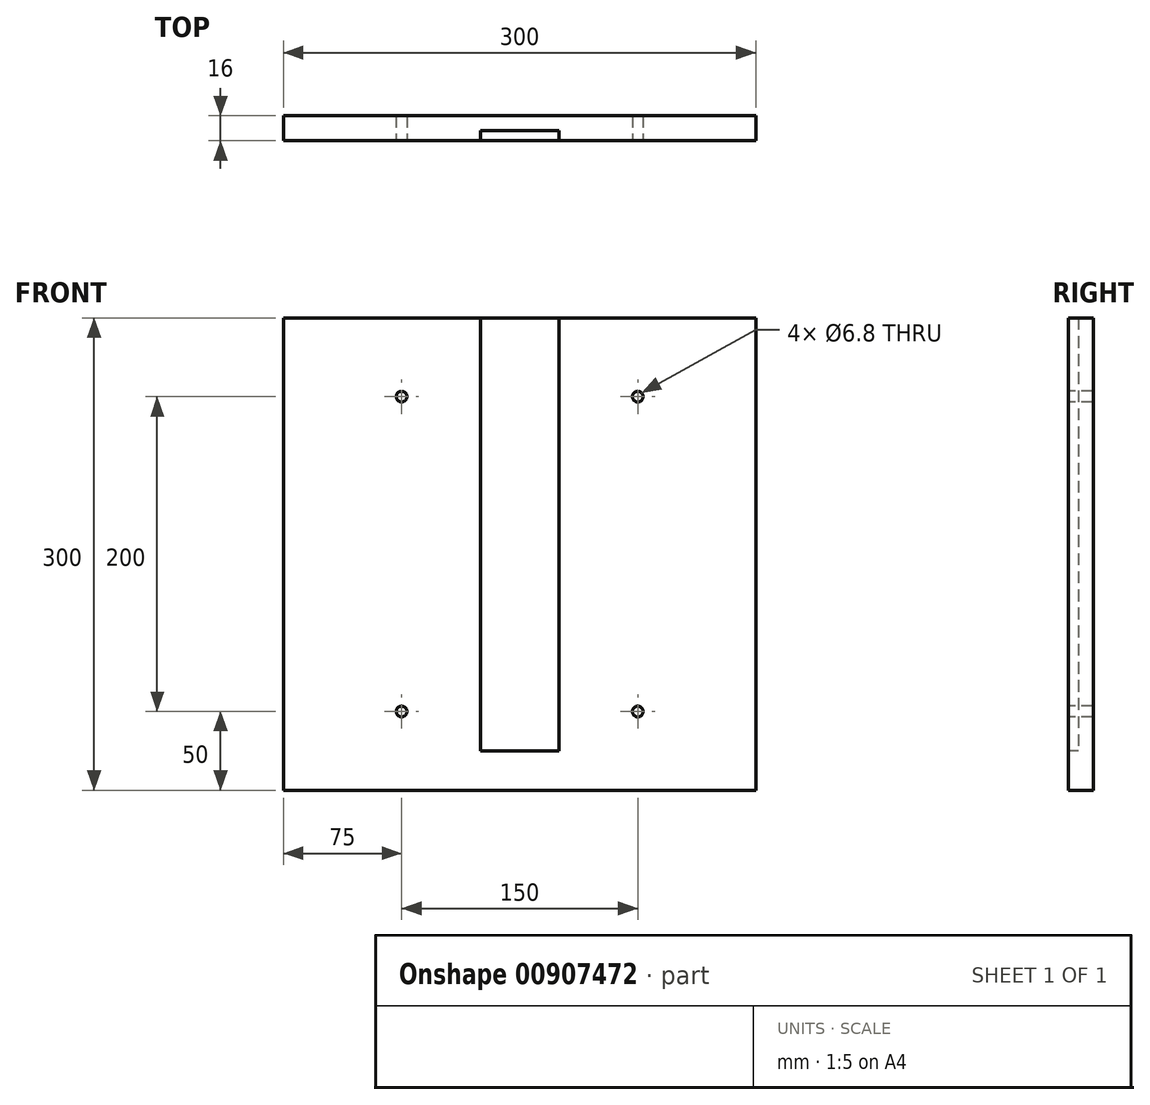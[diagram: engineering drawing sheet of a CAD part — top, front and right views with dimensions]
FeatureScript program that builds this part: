
annotation { "Feature Type Name" : "Feature", "Feature Type Description" : "" }
export const myFeature = defineFeature(function(context is Context, id is Id, definition is map)
    precondition{}
    {
        {
            var Q0;
            Q0=qCreatedBy(makeId("Front.planeOp"),FACE);
            var sketch = newSketch(context, id + "F0", { "sketchPlane" : qUnion([Q0])});
            skLineSegment(sketch, "E0.bottom", {"start": v(-155, 150) * mm, "end": v(155, 150) * mm});
            skLineSegment(sketch, "E0.top", {"start": v(-155, -150) * mm, "end": v(155, -150) * mm});
            skLineSegment(sketch, "E0.left", {"start": v(-155, 150) * mm, "end": v(-155, -150) * mm});
            skLineSegment(sketch, "E0.right", {"start": v(155, 150) * mm, "end": v(155, -150) * mm});
            skLineSegment(sketch, "E1", {"start": v(-155, 150) * mm, "end": v(155, -150) * mm, "construction": true});
            skSolve(sketch);
        }
        {
            var Q0;
            Q0=makeQuery(id+"F0.imprint","IMPRINT",FACE,{"disambiguationData":[TD([[makeQuery(id+"F0.imprint","IMPRINT",EDGE,{"derivedFrom":sQuery(id+"F0.wireOp",EDGE,"E0.bottom")}),-1.0]])]});
            extrude(context, id + "F1", {"entities" : qUnion([Q0]), "depth" : 16 * mm, "offsetDistance" : 25 * mm});
        }
        {
            var Q0;
            Q0=makeQuery(id+"F1.opExtrude","CAP_FACE",FACE,{"disambiguationData":[OSD([sQuery(id+"F0.wireOp",EDGE,"E0.bottom"),sQuery(id+"F0.wireOp",EDGE,"E0.top"),sQuery(id+"F0.wireOp",EDGE,"E0.left"),sQuery(id+"F0.wireOp",EDGE,"E0.right")])],"isStart":false});
            var sketch = newSketch(context, id + "F2", { "sketchPlane" : qUnion([Q0])});
            skLineSegment(sketch, "E2.bottom", {"start": v(155, 150) * mm, "end": v(150, 150) * mm});
            skLineSegment(sketch, "E2.top", {"start": v(155, -150) * mm, "end": v(150, -150) * mm});
            skLineSegment(sketch, "E2.left", {"start": v(155, 150) * mm, "end": v(155, -150) * mm});
            skLineSegment(sketch, "E2.right", {"start": v(150, 150) * mm, "end": v(150, -150) * mm});
            skLineSegment(sketch, "E3.bottom", {"start": v(-155, -150) * mm, "end": v(-150, -150) * mm});
            skLineSegment(sketch, "E3.top", {"start": v(-155, 150) * mm, "end": v(-150, 150) * mm});
            skLineSegment(sketch, "E3.left", {"start": v(-155, -150) * mm, "end": v(-155, 150) * mm});
            skLineSegment(sketch, "E3.right", {"start": v(-150, -150) * mm, "end": v(-150, 150) * mm});
            skSolve(sketch);
        }
        {
            var Q0;
            Q0 = qSketchRegion(id + "F2", true);
            extrude(context, id + "F3", {"entities" : qUnion([Q0]), "operationType" : NewBodyOperationType.REMOVE, "endBound" : BoundingType.THROUGH_ALL, "oppositeDirection" : true, "depth" : 25 * mm, "offsetDistance" : 25 * mm});
        }
        {
            var Q0;
            Q0=makeQuery(id+"F1.opExtrude","CAP_FACE",FACE,{"disambiguationData":[OSD([sQuery(id+"F0.wireOp",EDGE,"E0.bottom"),sQuery(id+"F0.wireOp",EDGE,"E0.top"),sQuery(id+"F0.wireOp",EDGE,"E0.left"),sQuery(id+"F0.wireOp",EDGE,"E0.right")])],"isStart":false});
            var sketch = newSketch(context, id + "F4", { "sketchPlane" : qUnion([Q0])});
            skLineSegment(sketch, "E4.bottom", {"start": v(-25, 150) * mm, "end": v(25, 150) * mm});
            skLineSegment(sketch, "E4.top", {"start": v(-25, -125) * mm, "end": v(25, -125) * mm});
            skLineSegment(sketch, "E4.left", {"start": v(-25, 150) * mm, "end": v(-25, -125) * mm});
            skLineSegment(sketch, "E4.right", {"start": v(25, 150) * mm, "end": v(25, -125) * mm});
            skSolve(sketch);
        }
        {
            var Q0;
            Q0 = qSketchRegion(id + "F4", true);
            extrude(context, id + "F5", {"entities" : qUnion([Q0]), "operationType" : NewBodyOperationType.REMOVE, "oppositeDirection" : true, "depth" : 6.5 * mm, "offsetDistance" : 25 * mm});
        }
        {
            var Q0;
            Q0=makeQuery(id+"F1.opExtrude","CAP_FACE",FACE,{"disambiguationData":[OSD([sQuery(id+"F0.wireOp",EDGE,"E0.bottom"),sQuery(id+"F0.wireOp",EDGE,"E0.top"),sQuery(id+"F0.wireOp",EDGE,"E0.left"),sQuery(id+"F0.wireOp",EDGE,"E0.right")])],"isStart":false});
            var sketch = newSketch(context, id + "F6", { "sketchPlane" : qUnion([Q0])});
            skPoint(sketch, "E5", {"position": v(-75, 100) * mm});
            skPoint(sketch, "E6", {"position": v(75, 100) * mm});
            skPoint(sketch, "E7", {"position": v(75, -100) * mm});
            skPoint(sketch, "E8", {"position": v(-75, -100) * mm});
            skLineSegment(sketch, "E9.bottom", {"start": v(-75, 100) * mm, "end": v(75, 100) * mm, "construction": true});
            skLineSegment(sketch, "E9.top", {"start": v(-75, -100) * mm, "end": v(75, -100) * mm, "construction": true});
            skLineSegment(sketch, "E9.left", {"start": v(-75, 100) * mm, "end": v(-75, -100) * mm, "construction": true});
            skLineSegment(sketch, "E9.right", {"start": v(75, 100) * mm, "end": v(75, -100) * mm, "construction": true});
            skSolve(sketch);
        }
        {
            var Q0;
            Q0=sQuery(id+"F6.wireOp",VERTEX,"E5");
            var Q1;
            Q1=sQuery(id+"F6.wireOp",VERTEX,"E6");
            var Q2;
            Q2=sQuery(id+"F6.wireOp",VERTEX,"E7");
            var Q3;
            Q3=sQuery(id+"F6.wireOp",VERTEX,"E8");
            var Q4;
            Q4=makeQuery(id+"F1.opExtrude","SWEPT_BODY",BODY,{"disambiguationData":[OSD([sQuery(id+"F0.wireOp",EDGE,"E0.bottom"),sQuery(id+"F0.wireOp",EDGE,"E0.top"),sQuery(id+"F0.wireOp",EDGE,"E0.left"),sQuery(id+"F0.wireOp",EDGE,"E0.right")])]});
            hole(context, id + "F7", {"style" : HoleStyle.SIMPLE, "endStyle" : HoleEndStyle.BLIND, "standardTappedOrClearance" : lookupTablePath({ "standard" : "ISO", "engagement" : "75%", "pitch" : "1.25 mm", "size" : "M8", "type" : "Tapped" }), "standardBlindInLast" : lookupTablePath({ "standard" : "ISO", "engagement" : "75%", "pitch" : "1.25 mm", "size" : "M8", "type" : "Tapped" }), "holeDiameter" : 6.8 * mm, "majorDiameter" : 8 * mm, "showTappedDepth" : true, "holeDepth" : 20 * mm, "isTappedThrough" : true, "tappedDepth" : 16.25 * mm, "tapClearance" : 3, "locations" : qUnion([Q0, Q1, Q2, Q3]), "scope" : qUnion([Q4])});
        }
    });
